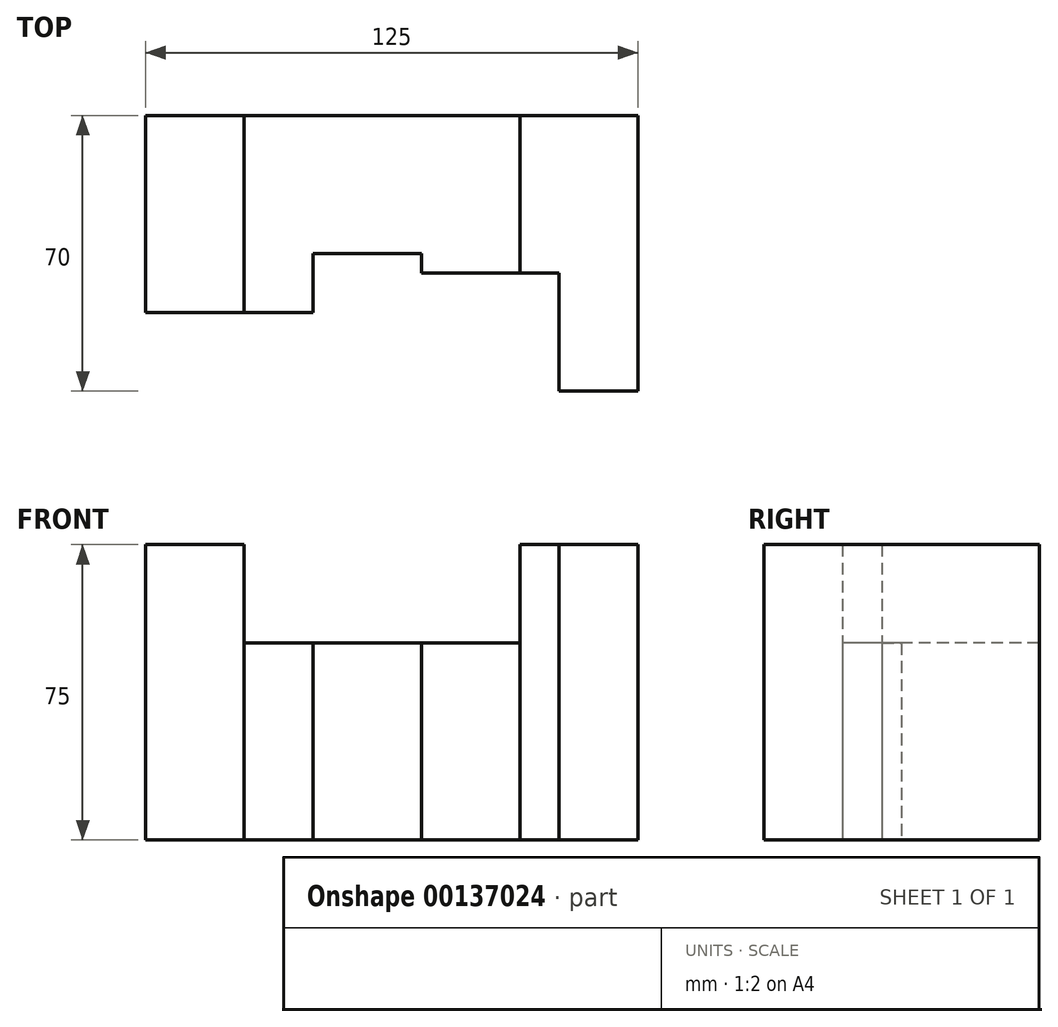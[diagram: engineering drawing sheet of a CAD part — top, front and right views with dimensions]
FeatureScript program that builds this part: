
annotation { "Feature Type Name" : "Feature", "Feature Type Description" : "" }
export const myFeature = defineFeature(function(context is Context, id is Id, definition is map)
    precondition{}
    {
        {
            var Q0;
            Q0=qCreatedBy(makeId("Top.planeOp"),FACE);
            var sketch = newSketch(context, id + "F0", { "sketchPlane" : qUnion([Q0])});
            skLineSegment(sketch, "E0", {"start": v(0, 0) * mm, "end": v(0, 50) * mm});
            skLineSegment(sketch, "E1", {"start": v(0, 50) * mm, "end": v(125, 50) * mm});
            skLineSegment(sketch, "E2", {"start": v(125, 50) * mm, "end": v(125, -20) * mm});
            skLineSegment(sketch, "E3", {"start": v(125, -20) * mm, "end": v(105, -20) * mm});
            skLineSegment(sketch, "E4", {"start": v(105, -20) * mm, "end": v(105, 10) * mm});
            skLineSegment(sketch, "E5", {"start": v(105, 10) * mm, "end": v(70, 10) * mm});
            skLineSegment(sketch, "E6", {"start": v(70, 10) * mm, "end": v(70, 15) * mm});
            skLineSegment(sketch, "E7", {"start": v(70, 15) * mm, "end": v(42.5, 15) * mm});
            skLineSegment(sketch, "E8", {"start": v(42.5, 15) * mm, "end": v(42.5, 0) * mm});
            skLineSegment(sketch, "E9", {"start": v(42.5, 0) * mm, "end": v(0, 0) * mm});
            skLineSegment(sketch, "E10", {"start": v(25, 50) * mm, "end": v(25, 0) * mm});
            skLineSegment(sketch, "E11", {"start": v(95, 50) * mm, "end": v(95, 10) * mm});
            skSolve(sketch);
        }
        {
            var Q0;
            {var subQ0=sQuery(id+"F0.wireOp",EDGE,"E0");Q0=makeQuery(id+"F0.imprint","IMPRINT",FACE,{"disambiguationData":[TD([[makeQuery(id+"F0.imprint","IMPRINT",EDGE,{"derivedFrom":subQ0}),-1.0]])]});}
            var Q1;
            {var subQ1=sQuery(id+"F0.wireOp",EDGE,"E2");Q1=makeQuery(id+"F0.imprint","IMPRINT",FACE,{"disambiguationData":[TD([[makeQuery(id+"F0.imprint","IMPRINT",EDGE,{"derivedFrom":subQ1}),-1.0]])]});}
            extrude(context, id + "F1", {"entities" : qUnion([Q0, Q1]), "depth" : (15 * 5) * mm});
        }
        {
            var Q0;
            {var subQ0=sQuery(id+"F0.wireOp",EDGE,"E6");Q0=makeQuery(id+"F0.imprint","IMPRINT",FACE,{"disambiguationData":[TD([[makeQuery(id+"F0.imprint","IMPRINT",EDGE,{"derivedFrom":subQ0}),-1.0]])]});}
            extrude(context, id + "F2", {"entities" : qUnion([Q0]), "depth" : 50 * mm});
        }
    });
